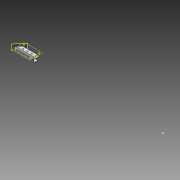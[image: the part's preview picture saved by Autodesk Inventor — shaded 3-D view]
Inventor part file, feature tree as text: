
AUTODESK INVENTOR PART (.ipt)
format: ipt  version: 2014 SP1 (Build 180222100, 222)  size: 217,600 bytes
history: native  units: in
note: dims shown in document units (in); Inventor stores cm internally (conversion verified against a paired STEP export)
features: sketch x8, extrude x6, hole x3, projected_geometry x3, reference x2, pattern_linear x1, plane x1
ambient origin geometry x8: Origin, YZ Plane, XZ Plane, XY Plane, X Axis, Y Axis, Z Axis, Center Point
bodies: Solid1 (feature_tree)
feature tree (24):
  extrude  "Extrusion1"  Depth=0.125in
  sketch  "Sketch2"  dims[d2=1.0in d3=1.0in]
  hole  "Hole1"  [1 undecoded]
  hole  "Hole2"  [1 undecoded]
  hole  "Hole3"  [1 undecoded]
  pattern_linear  "Rectangular Pattern1"  Count1=2 Spacing1=10.0in
  extrude  "Extrusion2"  Depth=1.0in
  extrude  "Extrusion3"  Depth=1.0in
  plane  "Work Plane1"
  extrude  "Extrusion4"  Depth=1.0in
  extrude  "Extrusion5"  Depth=1.0in TaperAngle=0.0deg
  extrude  "Extrusion6"  Depth=1.0in TaperAngle=0.0deg
  sketch  "Sketch1"  dims[d0=1.125in d1=0.125in]
  sketch  "Sketch3"  dims[d4=0.125in d5=0.125in]
  sketch  "Sketch4"  dims[d6=0.25in d7=35.0in d8=0.0in]
  sketch  "Sketch5"  dims[d10=0.3in]
  reference  "Reference1"
  sketch  "Sketch6"  dims[d11=0.15in d12=0.7874in d14=10.0in d15=0.3937in d17=1.0in]
  projected_geometry  "Projected Loop1"
  projected_geometry  "Projected Loop2"
  projected_geometry  "Projected Loop3"
  sketch  "Sketch7"  dims[d20=0.38in d21=0.75in d22=0.375in d23=0.25in d24=0.5635in d25=1.0in d26=0.8108in]
  sketch  "Sketch8"  dims[d27=0.125in d28=0.75in d29=0.375in d30=0.25in d31=0.5635in d32=1.0in d33=0.8108in d34=0.5in d35=0.5in d36=0.257in d37=0.75in d38=0.375in d39=0.25in d40=0.5635in d41=1.0in d42=0.8108in d43=13.7795in d45=1.0in d46=30.5in d47=0.0in d51=1.0in d52=0.0in d53=0.3436in d54=1.25in d55=2.0in d56=0.75in d57=0.5in d58=0.0in d59=0.125in d60=3.7507in d61=0.6875in d62=0.0in d63=1.0in d64=0.0in]
  reference  "Reference2"
note: 3 required parameter values undecoded (feature->parameter linkage not recoverable at this tier; creation-order binding heuristic only, values carry confidence <= 0.55)
